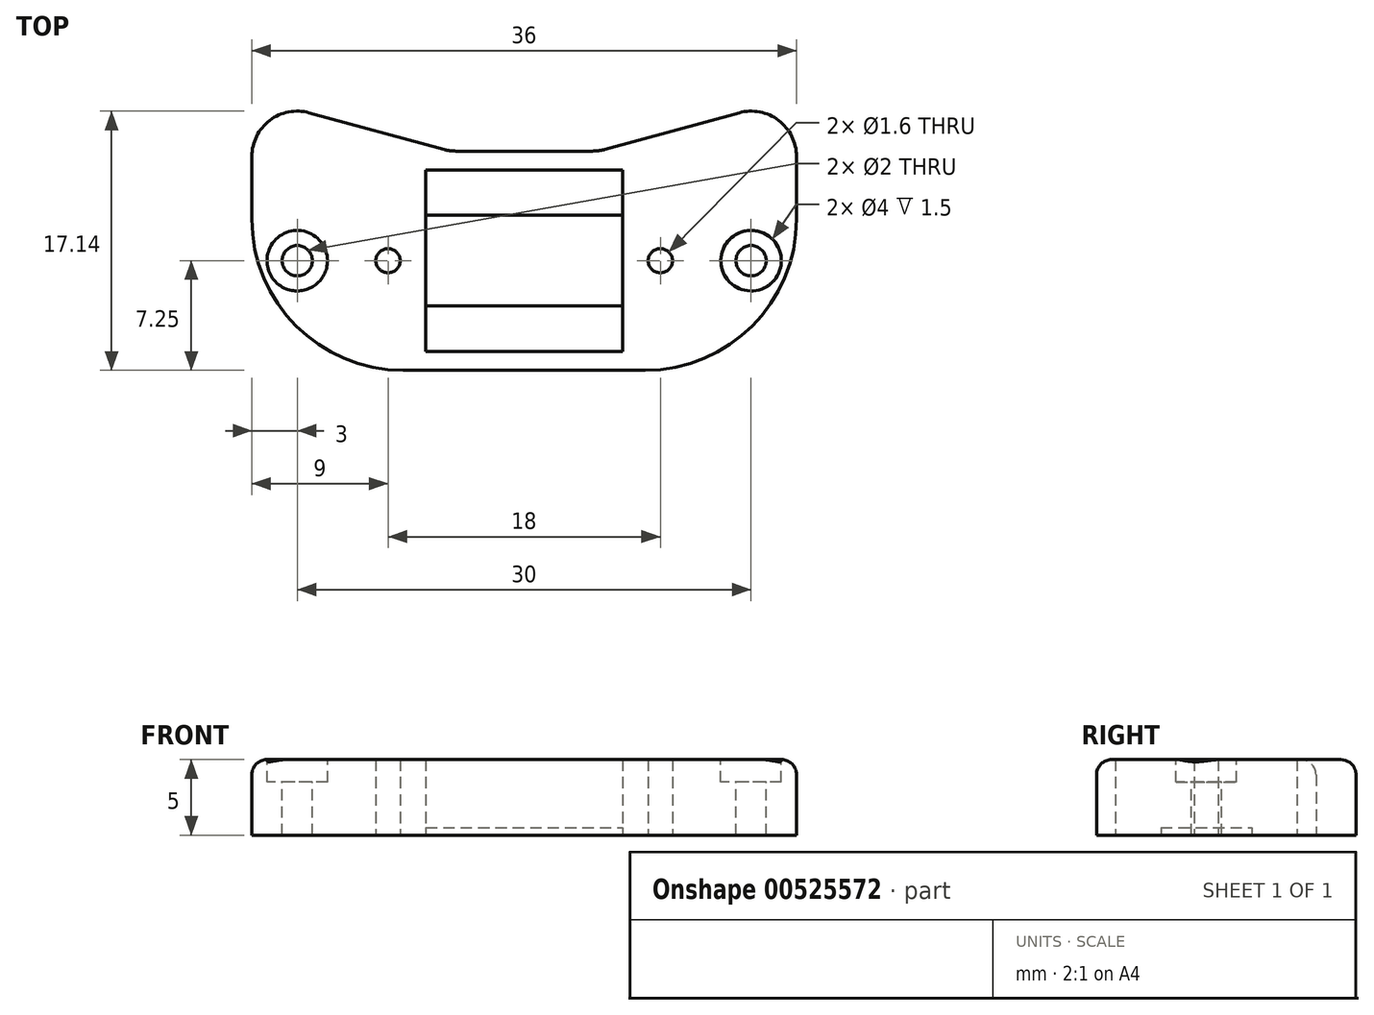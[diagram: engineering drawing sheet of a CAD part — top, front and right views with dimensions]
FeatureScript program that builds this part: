
annotation { "Feature Type Name" : "Feature", "Feature Type Description" : "" }
export const myFeature = defineFeature(function(context is Context, id is Id, definition is map)
    precondition{}
    {
        {
            var Q0;
            Q0=qCreatedBy(makeId("Top.planeOp"),FACE);
            var sketch = newSketch(context, id + "F0", { "sketchPlane" : qUnion([Q0])});
            skLineSegment(sketch, "E0.bottom", {"start": v(18, -7.25) * mm, "end": v(-18, -7.25) * mm});
            skLineSegment(sketch, "E0.top", {"start": v(18, 7.25) * mm, "end": v(-18, 7.25) * mm});
            skLineSegment(sketch, "E0.left", {"start": v(18, -7.25) * mm, "end": v(18, 7.25) * mm});
            skLineSegment(sketch, "E0.right", {"start": v(-18, -7.25) * mm, "end": v(-18, 7.25) * mm});
            skPoint(sketch, "E0.middle", {"position": v(0, 0) * mm});
            skLineSegment(sketch, "E1.bottom", {"start": v(6.5, -6) * mm, "end": v(-6.5, -6) * mm});
            skLineSegment(sketch, "E1.top", {"start": v(6.5, 6) * mm, "end": v(-6.5, 6) * mm});
            skLineSegment(sketch, "E1.left", {"start": v(6.5, -6) * mm, "end": v(6.5, 6) * mm});
            skLineSegment(sketch, "E1.right", {"start": v(-6.5, -6) * mm, "end": v(-6.5, 6) * mm});
            skCircle(sketch, "E2", {"center": v(-9, 0) * mm, "radius": 0.8 * mm});
            skCircle(sketch, "E3", {"center": v(9, 0) * mm, "radius": 0.8 * mm});
            skLineSegment(sketch, "E4", {"start": v(-16.5, 10.41) * mm, "end": v(-4.93, 7.25) * mm});
            skLineSegment(sketch, "E5", {"start": v(0, 18.48) * mm, "end": v(0, 14.95) * mm, "construction": true});
            skArc(sketch, "E6", {"start": v(-16.5, 10.41) * mm, "mid": v(-17.6, 9) * mm, "end": v(-18, 7.25) * mm});
            skLineSegment(sketch, "E7.MirrorCS", {"start": v(16.5, 10.41) * mm, "end": v(4.93, 7.25) * mm});
            skArc(sketch, "E8.MirrorCS", {"start": v(16.5, 10.41) * mm, "mid": v(17.6, 9) * mm, "end": v(18, 7.25) * mm});
            skSolve(sketch);
        }
        {
            var Q0;
            Q0 = qSketchRegion(id + "F0", true);
            extrude(context, id + "F1", {"entities" : qUnion([Q0]), "depth" : 5 * mm, "offsetDistance" : 25 * mm});
        }
        {
            var Q0;
            Q0=makeQuery(id+"F1.opExtrude","CAP_FACE",FACE,{"disambiguationData":[OSD([sQuery(id+"F0.wireOp",EDGE,"E0.bottom"),sQuery(id+"F0.wireOp",EDGE,"E0.top"),sQuery(id+"F0.wireOp",EDGE,"E0.left"),sQuery(id+"F0.wireOp",EDGE,"E0.right"),sQuery(id+"F0.wireOp",EDGE,"E1.bottom"),sQuery(id+"F0.wireOp",EDGE,"E1.top"),sQuery(id+"F0.wireOp",EDGE,"E1.left"),sQuery(id+"F0.wireOp",EDGE,"E1.right")])],"isStart":true});
            var sketch = newSketch(context, id + "F2", { "sketchPlane" : qUnion([Q0])});
            skLineSegment(sketch, "E9.bottom", {"start": v(-6.5, -3) * mm, "end": v(6.5, -3) * mm});
            skLineSegment(sketch, "E9.top", {"start": v(-6.5, 3) * mm, "end": v(6.5, 3) * mm});
            skLineSegment(sketch, "E9.left", {"start": v(-6.5, -3) * mm, "end": v(-6.5, 3) * mm});
            skLineSegment(sketch, "E9.right", {"start": v(6.5, -3) * mm, "end": v(6.5, 3) * mm});
            skPoint(sketch, "E9.middle", {"position": v(0, 0) * mm});
            skSolve(sketch);
        }
        {
            var Q0;
            Q0 = qSketchRegion(id + "F2", true);
            extrude(context, id + "F3", {"entities" : qUnion([Q0]), "operationType" : NewBodyOperationType.ADD, "oppositeDirection" : true, "depth" : 0.5 * mm, "offsetDistance" : 25 * mm});
        }
        {
            var Q0;
            Q0=makeQuery(id+"F1.opExtrude","CAP_FACE",FACE,{"disambiguationData":[OSD([sQuery(id+"F0.wireOp",EDGE,"E0.bottom"),sQuery(id+"F0.wireOp",EDGE,"E0.top"),sQuery(id+"F0.wireOp",EDGE,"E0.left"),sQuery(id+"F0.wireOp",EDGE,"E0.right"),sQuery(id+"F0.wireOp",EDGE,"E1.bottom"),sQuery(id+"F0.wireOp",EDGE,"E1.top"),sQuery(id+"F0.wireOp",EDGE,"E1.left"),sQuery(id+"F0.wireOp",EDGE,"E1.right"),sQuery(id+"F0.wireOp",EDGE,"E2"),sQuery(id+"F0.wireOp",EDGE,"E3")])],"isStart":false});
            var sketch = newSketch(context, id + "F4", { "sketchPlane" : qUnion([Q0])});
            skPoint(sketch, "E10", {"position": v(-15, 0) * mm});
            skPoint(sketch, "E11", {"position": v(15, 0) * mm});
            skSolve(sketch);
        }
        {
            var Q0;
            Q0=sQuery(id+"F4.wireOp",VERTEX,"E10");
            var Q1;
            Q1=sQuery(id+"F4.wireOp",VERTEX,"E11");
            var Q2;
            Q2=makeQuery(id+"F1.opExtrude","SWEPT_BODY",BODY,{"disambiguationData":[OSD([sQuery(id+"F0.wireOp",EDGE,"E0.bottom"),sQuery(id+"F0.wireOp",EDGE,"E0.top"),sQuery(id+"F0.wireOp",EDGE,"E0.left"),sQuery(id+"F0.wireOp",EDGE,"E0.right"),sQuery(id+"F0.wireOp",EDGE,"E1.bottom"),sQuery(id+"F0.wireOp",EDGE,"E1.top"),sQuery(id+"F0.wireOp",EDGE,"E1.left"),sQuery(id+"F0.wireOp",EDGE,"E1.right"),sQuery(id+"F0.wireOp",EDGE,"E2"),sQuery(id+"F0.wireOp",EDGE,"E3")])]});
            hole(context, id + "F5", {"style" : HoleStyle.C_BORE, "endStyle" : HoleEndStyle.BLIND, "holeDiameter" : 2 * mm, "cBoreDiameter" : 4 * mm, "cBoreDepth" : 1.5 * mm, "majorDiameter" : 5 * mm, "holeDepth" : 20 * mm, "tappedDepth" : 12 * mm, "tapClearance" : 3, "locations" : qUnion([Q0, Q1]), "scope" : qUnion([Q2])});
        }
        {
            var Q0;
            Q0=makeQuery(id+"F1.opExtrude","SWEPT_EDGE",EDGE,{"disambiguationData":[OSD([sQuery(id+"F0.wireOp",EDGE,"E0.bottom"),sQuery(id+"F0.wireOp",EDGE,"E0.right")])]});
            var Q1;
            Q1=makeQuery(id+"F1.opExtrude","SWEPT_EDGE",EDGE,{"disambiguationData":[OSD([sQuery(id+"F0.wireOp",EDGE,"E0.bottom"),sQuery(id+"F0.wireOp",EDGE,"E0.left")])]});
            fillet(context, id + "F6", {"entities" : qUnion([Q0, Q1]), "radius" : 10 * mm, "tangentPropagation" : true, "allowEdgeOverflow" : false});
        }
        {
            var Q0;
            Q0=makeQuery(id+"F1.opExtrude","SWEPT_EDGE",EDGE,{"disambiguationData":[OSD([sQuery(id+"F0.wireOp",EDGE,"E4"),sQuery(id+"F0.wireOp",EDGE,"E6")])]});
            var Q1;
            Q1=makeQuery(id+"F1.opExtrude","SWEPT_EDGE",EDGE,{"disambiguationData":[OSD([sQuery(id+"F0.wireOp",EDGE,"E7.MirrorCS"),sQuery(id+"F0.wireOp",EDGE,"E8.MirrorCS")])]});
            var Q2;
            Q2=makeQuery(id+"F1.opExtrude","SWEPT_EDGE",EDGE,{"disambiguationData":[OSD([sQuery(id+"F0.wireOp",EDGE,"E0.top"),sQuery(id+"F0.wireOp",EDGE,"E4")])]});
            var Q3;
            Q3=makeQuery(id+"F1.opExtrude","SWEPT_EDGE",EDGE,{"disambiguationData":[OSD([sQuery(id+"F0.wireOp",EDGE,"E0.top"),sQuery(id+"F0.wireOp",EDGE,"E7.MirrorCS")])]});
            fillet(context, id + "F7", {"entities" : qUnion([Q0, Q1, Q2, Q3]), "radius" : 3 * mm, "tangentPropagation" : true, "allowEdgeOverflow" : false});
        }
        {
            var Q0;
            {var subQ0=sQuery(id+"F0.wireOp",EDGE,"E0.left");var subQ1=sQuery(id+"F0.wireOp",EDGE,"E0.bottom");Q0=makeQuery(id+"F6.opFillet","BLEND_EDGE",EDGE,{"blendedFrom":[makeQuery(id+"F1.opExtrude","SWEPT_EDGE",EDGE,{"disambiguationData":[OSD([subQ1,subQ0])]}),makeQuery(id+"F1.opExtrude","CAP_FACE",FACE,{"disambiguationData":[OSD([subQ1,sQuery(id+"F0.wireOp",EDGE,"E0.top"),subQ0,sQuery(id+"F0.wireOp",EDGE,"E0.right"),sQuery(id+"F0.wireOp",EDGE,"E1.bottom"),sQuery(id+"F0.wireOp",EDGE,"E1.top"),sQuery(id+"F0.wireOp",EDGE,"E1.left"),sQuery(id+"F0.wireOp",EDGE,"E1.right"),sQuery(id+"F0.wireOp",EDGE,"E2"),sQuery(id+"F0.wireOp",EDGE,"E3"),sQuery(id+"F0.wireOp",EDGE,"E4"),sQuery(id+"F0.wireOp",EDGE,"E6"),sQuery(id+"F0.wireOp",EDGE,"E7.MirrorCS"),sQuery(id+"F0.wireOp",EDGE,"E8.MirrorCS")])],"isStart":false})],"blendedInto":[makeQuery(id+"F1.opExtrude","CAP_FACE",FACE,{"disambiguationData":[OSD([subQ1,sQuery(id+"F0.wireOp",EDGE,"E0.top"),subQ0,sQuery(id+"F0.wireOp",EDGE,"E0.right"),sQuery(id+"F0.wireOp",EDGE,"E1.bottom"),sQuery(id+"F0.wireOp",EDGE,"E1.top"),sQuery(id+"F0.wireOp",EDGE,"E1.left"),sQuery(id+"F0.wireOp",EDGE,"E1.right"),sQuery(id+"F0.wireOp",EDGE,"E2"),sQuery(id+"F0.wireOp",EDGE,"E3"),sQuery(id+"F0.wireOp",EDGE,"E4"),sQuery(id+"F0.wireOp",EDGE,"E6"),sQuery(id+"F0.wireOp",EDGE,"E7.MirrorCS"),sQuery(id+"F0.wireOp",EDGE,"E8.MirrorCS")])],"isStart":false})]});}
            fillet(context, id + "F8", {"entities" : qUnion([Q0]), "radius" : 1 * mm, "tangentPropagation" : true, "allowEdgeOverflow" : false});
        }
    });
